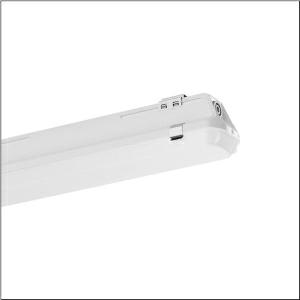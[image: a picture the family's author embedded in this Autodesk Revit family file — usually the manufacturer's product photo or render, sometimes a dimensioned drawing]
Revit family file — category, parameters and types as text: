
# Revit family: monsun_r__11_51fp207p4b0q_e68d
name_source: partatom
category: Lighting Fixtures
units: mm (PartAtom-declared; Revit-internal decimal feet)

## family parameters
Cut with Voids When Loaded = No
Host = Face
Light Source = No
Part Type = Normal
Room Calculation Point = No
Round Connector Dimension = Use Diameter
Shared = No

## types (1)
- Monsun® 11 (1 x LED, 10910 lm, 66.2 W, 4000K)
    Apparent Load = 66 VA
    CIE Flux Codes = 45 75 93 94 100
    Color Rendering = 80
    Color Temperature = 4000K
    Default Elevation = 1800 mm
    Description = Monsun® 11, damp-proof luminaire, chain hanger, primary optical cover: enclosure, of PC, light emission: direct distribution, primary light characteristic: symmetric, installation type: suspended mounting, surface-mounted, horizontal mounting, vertical mounting, LED, rated luminous flux: 10.910lm, luminous efficacy: 165lm/W, light colour: 840, colour temperature: 4000K, control gear: ECG, with terminal, 3-pole, max. 2.5mm², mains connection: 220..240V, AC, 50/60Hz, rated input power: 66W, luminaire housing, of glass-fibre reinforced polyester, uncoated, bright grey, incl. chain hanger, length: 1.590mm, width: 90mm, height: 88mm, clip for enclosure, of stainless steel (V2A), ceiling mounting element, of stainless steel (V2A), chain hanger, of stainless steel (V2A), protection rating (complete): IP66, insulation class (complete): insulation class I (protective earthing), certification: CE, ENEC, VDE, UKCA, protection symbol: D, impact resistance: IK08, permissible operating ambient temperature: -35..+35°C, standard: EN 50419, EN 60598-2-1, no direct snow, no direct sun, no direct rain, for indoor or canopied outdoor use, corresponds to IFS (International Featured Standards) requirements for safety and quality in the food industry, contact your sales advisor before using the luminaires in applications with unclear chemical exposure, large temperature fluctuations or condensation-forming humidity, LABS conformity tested according to VDMA 24364:2018-05, packaging unit: 1 piece
    Height = 89 mm
    Lamp = 1 x LED
    Lamp Light Flux = 10910 lm
    Lamp Power = 66.2 W
    Lamp count = 1
    Length = 1590 mm
    Luminous efficacy = 165 lm/W
    Manufacturer = Siteco
    ModVariant = No
    Model = 51FP207P4B0Q
    Mounting Place = Ceiling
    Mounting Type = Surface mounted
    Number of Poles = 1
    OnlyDefault = Yes
    Power Factor = 1
    Product Name = Monsun® 11
    Product group = damp-proof luminaire
    ProductGroupID = 300
    Protection Class = Protection class I
    Protection Degree = IP 66
    RLX_Detail_Level = 1
    RLX_Emergency_Light_Flux = 0 lm
    RLX_Emergency_Type = 0
    RLX_Emergency_Type_DB = No
    RlxData = <blob elided: 88617 chars, md5=1da5feb0>
    Socket = socket
    Standby Power = 0 W
    System Light Flux = 10910 lm
    System Power = 66 W
    Type Comments = Product without accessories
    Type Image = l_1004748.jpg
    URL = http://relux.com
    VarID = ---
    Voltage = 0 V
    Weight = 0.00 kg
    Width = 90 mm

## geometry (parser evidence)
native form markers: Blend x4, Sweep x13
no freeform markers — native parametric forms only
